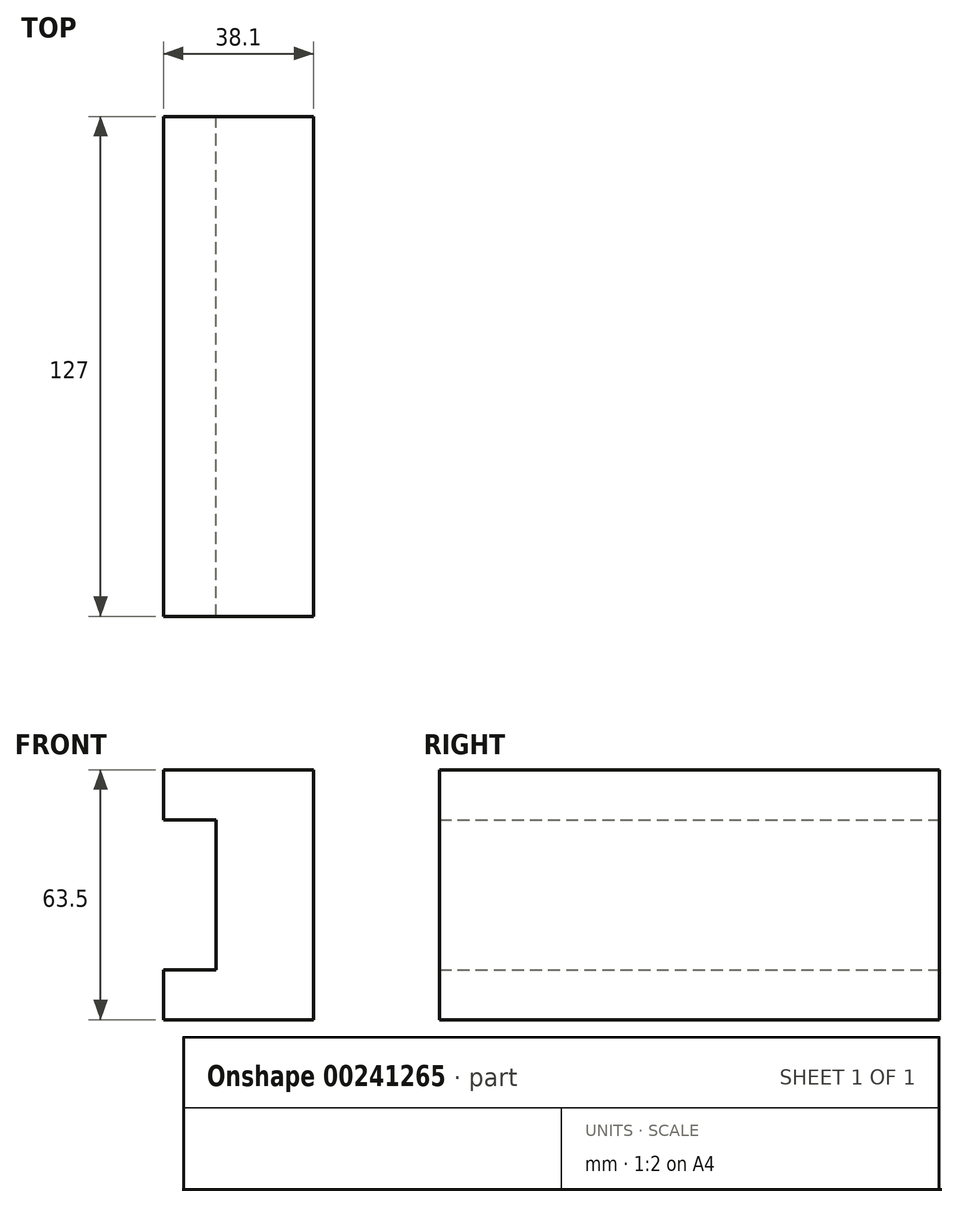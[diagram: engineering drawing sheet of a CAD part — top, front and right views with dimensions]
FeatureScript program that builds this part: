
annotation { "Feature Type Name" : "Feature", "Feature Type Description" : "" }
export const myFeature = defineFeature(function(context is Context, id is Id, definition is map)
    precondition{}
    {
        {
            var Q0;
            Q0=qCreatedBy(makeId("Front.planeOp"),FACE);
            var sketch = newSketch(context, id + "F0", { "sketchPlane" : qUnion([Q0])});
            skLineSegment(sketch, "E0", {"start": v(0, 0) * mm, "end": v(38.1, 0) * mm});
            skLineSegment(sketch, "E1", {"start": v(38.1, 0) * mm, "end": v(38.1, 63.5) * mm});
            skLineSegment(sketch, "E2", {"start": v(38.1, 63.5) * mm, "end": v(0, 63.5) * mm});
            skLineSegment(sketch, "E3", {"start": v(0, 63.5) * mm, "end": v(0, 50.8) * mm});
            skLineSegment(sketch, "E4", {"start": v(13.3, 50.8) * mm, "end": v(13.3, 12.7) * mm});
            skLineSegment(sketch, "E5", {"start": v(13.3, 12.7) * mm, "end": v(0, 12.7) * mm});
            skLineSegment(sketch, "E6", {"start": v(0, 0) * mm, "end": v(0, 12.7) * mm});
            skLineSegment(sketch, "E7", {"start": v(0, 50.8) * mm, "end": v(13.3, 50.8) * mm});
            skSolve(sketch);
        }
        {
            var Q0;
            Q0=makeQuery(id+"F0.imprint","IMPRINT",FACE,{"disambiguationData":[TD([[makeQuery(id+"F0.imprint","IMPRINT",EDGE,{"derivedFrom":sQuery(id+"F0.wireOp",EDGE,"E0")}),1.0]])]});
            extrude(context, id + "F1", {"entities" : qUnion([Q0]), "depth" : 127 * mm});
        }
    });
